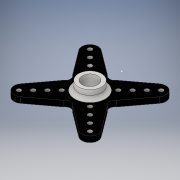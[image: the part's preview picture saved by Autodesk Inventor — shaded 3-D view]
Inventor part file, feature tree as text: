
AUTODESK INVENTOR PART (.ipt)
format: ipt  version: 2016 (Build 200138000, 138)  size: 230,912 bytes
history: native  units: in
note: dims shown in document units (in); Inventor stores cm internally (conversion verified against a paired STEP export)
features: sketch x2, pattern_circular x1, fillet x1, extrude x1
ambient origin geometry x8: Origin, YZ Plane, XZ Plane, XY Plane, X Axis, Y Axis, Z Axis, Center Point
bodies: Solid1 (feature_tree)
feature tree (5):
  pattern_circular  "CirPattern1"
  fillet  "Fillet1"  Radius=0.05in
  sketch  "Sketch1"  dims[d1=0.172in d2=0.0in]
  extrude  "Extrusion1"  [1 undecoded]
  sketch  "Sketch2"
note: 1 required parameter value undecoded (feature->parameter linkage not recoverable at this tier; creation-order binding heuristic only, values carry confidence <= 0.55)
